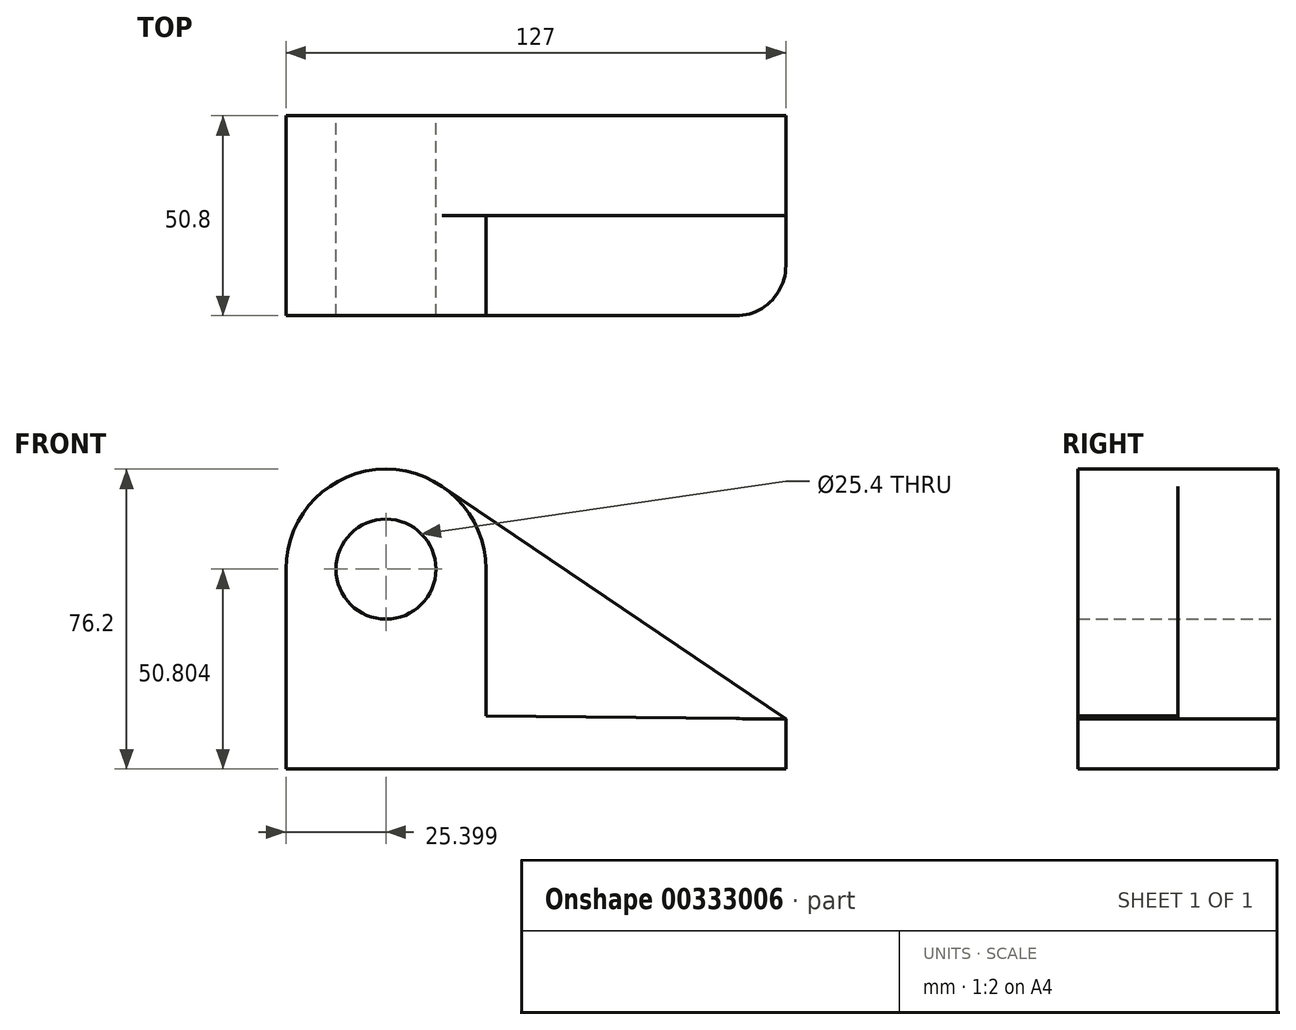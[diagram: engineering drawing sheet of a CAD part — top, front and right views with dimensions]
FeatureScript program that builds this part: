
annotation { "Feature Type Name" : "Feature", "Feature Type Description" : "" }
export const myFeature = defineFeature(function(context is Context, id is Id, definition is map)
    precondition{}
    {
        {
            var Q0;
            Q0=qCreatedBy(makeId("Front.planeOp"),FACE);
            var sketch = newSketch(context, id + "F0", { "sketchPlane" : qUnion([Q0])});
            skCircle(sketch, "E0", {"center": v(-57.56, 47.7) * mm, "radius": 12.7 * mm});
            skArc(sketch, "E1", {"start": v(-43.32, 68.74) * mm, "mid": v(-69.47, 70.14) * mm, "end": v(-82.96, 47.7) * mm});
            skLineSegment(sketch, "E2", {"start": v(-82.96, 47.7) * mm, "end": v(-82.96, -3.1) * mm});
            skLineSegment(sketch, "E3", {"start": v(-82.96, -3.1) * mm, "end": v(44.04, -3.1) * mm});
            skLineSegment(sketch, "E4", {"start": v(44.04, -3.1) * mm, "end": v(44.04, 9.6) * mm});
            skLineSegment(sketch, "E5", {"start": v(44.04, 9.6) * mm, "end": v(-43.32, 68.74) * mm});
            skSolve(sketch);
        }
        {
            var Q0;
            Q0=makeQuery(id+"F0.imprint","IMPRINT",FACE,{"disambiguationData":[TD([[makeQuery(id+"F0.imprint","IMPRINT",EDGE,{"derivedFrom":sQuery(id+"F0.wireOp",EDGE,"E0")}),-1.0]])]});
            extrude(context, id + "F1", {"entities" : qUnion([Q0]), "depth" : 25.4 * mm});
        }
        {
            var Q0;
            Q0=makeQuery(id+"F1.opExtrude","CAP_FACE",FACE,{"disambiguationData":[OSD([sQuery(id+"F0.wireOp",EDGE,"E0"),sQuery(id+"F0.wireOp",EDGE,"E1"),sQuery(id+"F0.wireOp",EDGE,"E2"),sQuery(id+"F0.wireOp",EDGE,"E3"),sQuery(id+"F0.wireOp",EDGE,"E4"),sQuery(id+"F0.wireOp",EDGE,"E5")])],"isStart":false});
            var sketch = newSketch(context, id + "F2", { "sketchPlane" : qUnion([Q0])});
            skCircle(sketch, "E6", {"center": v(-57.56, 47.7) * mm, "radius": 12.7 * mm});
            skLineSegment(sketch, "E7", {"start": v(44.04, 9.6) * mm, "end": v(-32.16, 10.37) * mm});
            skLineSegment(sketch, "E8", {"start": v(-32.16, 47.7) * mm, "end": v(-32.16, 10.37) * mm});
            skLineSegment(sketch, "E9", {"start": v(-57.56, 47.7) * mm, "end": v(-70.26, 47.7) * mm});
            skArc(sketch, "E10", {"start": v(-32.16, 47.7) * mm, "mid": v(-57.56, 73.1) * mm, "end": v(-82.96, 47.7) * mm});
            skSolve(sketch);
        }
        {
            var Q0;
            Q0=makeQuery(id+"F2.imprint","IMPRINT",FACE,{"disambiguationData":[TD([[makeQuery(id+"F2.imprint","IMPRINT",EDGE,{"derivedFrom":sQuery(id+"F2.wireOp",EDGE,"E6")}),-1.0]])]});
            extrude(context, id + "F3", {"entities" : qUnion([Q0]), "operationType" : NewBodyOperationType.ADD, "depth" : 25.4 * mm});
        }
        {
            var Q0;
            Q0=makeQuery(id+"F3.opExtrude","CAP_EDGE",EDGE,{"disambiguationData":[OSD([sQuery(id+"F0.wireOp",EDGE,"E4")])],"isStart":false});
            fillet(context, id + "F4", {"entities" : qUnion([Q0]), "radius" : 12.7 * mm, "tangentPropagation" : true, "allowEdgeOverflow" : false});
        }
    });
